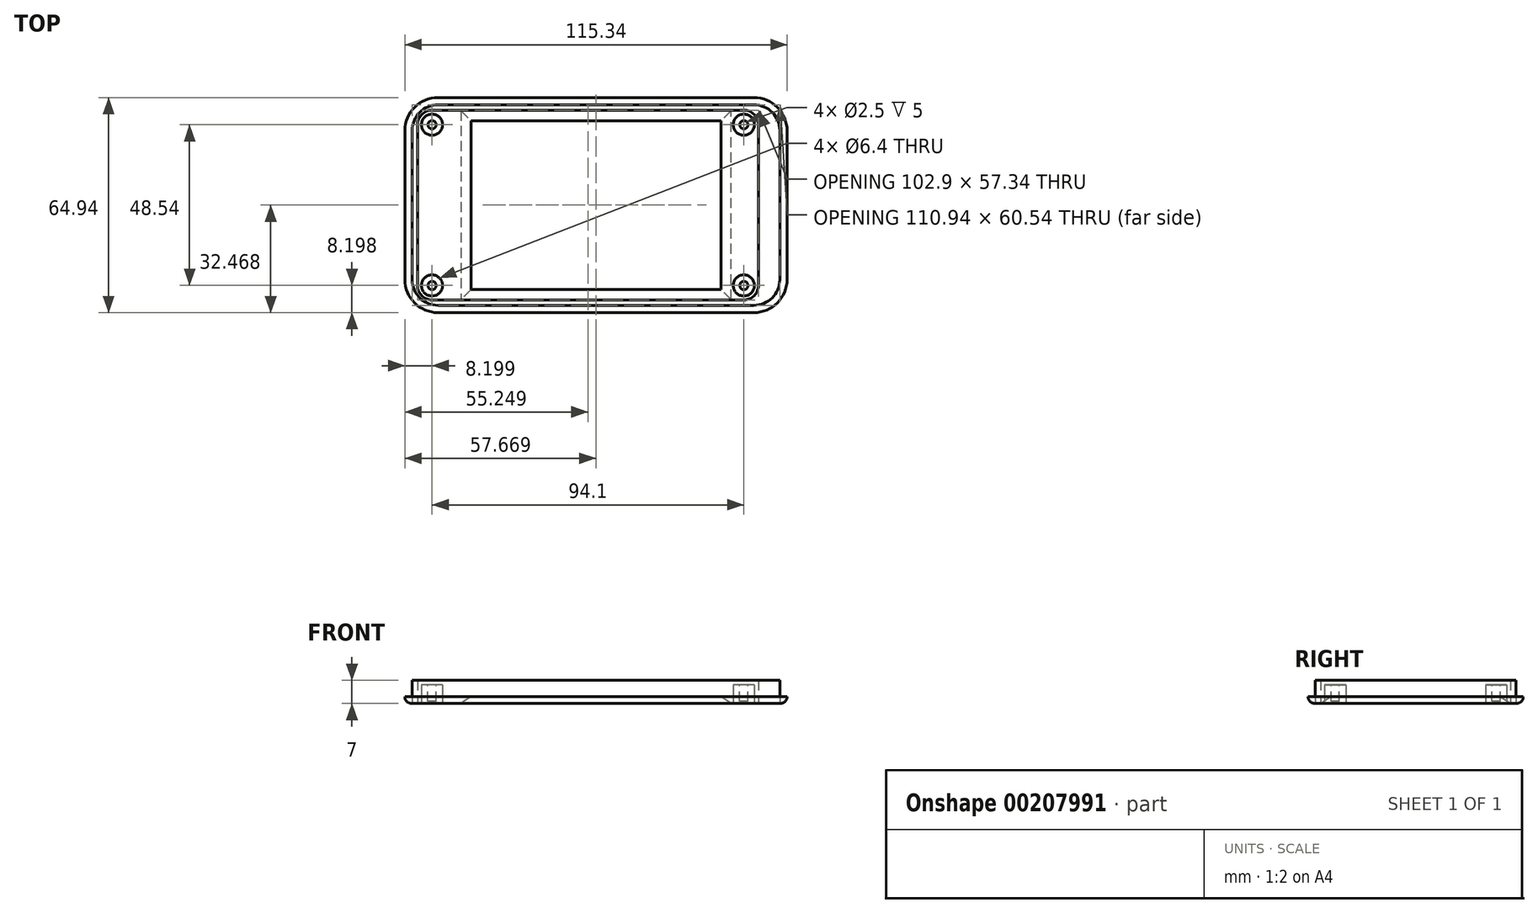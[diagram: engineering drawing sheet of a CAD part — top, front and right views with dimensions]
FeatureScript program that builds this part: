
annotation { "Feature Type Name" : "Feature", "Feature Type Description" : "" }
export const myFeature = defineFeature(function(context is Context, id is Id, definition is map)
    precondition{}
    {
        {
            var Q0;
            Q0=qCreatedBy(makeId("Top.planeOp"),FACE);
            var sketch = newSketch(context, id + "F0", { "sketchPlane" : qUnion([Q0])});
            skCircle(sketch, "E0", {"center": v(-31.24, 28.46) * mm, "radius": 3.2 * mm});
            skCircle(sketch, "E1", {"center": v(62.86, 28.46) * mm, "radius": 3.2 * mm});
            skCircle(sketch, "E2", {"center": v(62.86, -20.08) * mm, "radius": 3.2 * mm});
            skCircle(sketch, "E3", {"center": v(-31.24, -20.08) * mm, "radius": 3.2 * mm});
            skLineSegment(sketch, "E4.bottom", {"start": v(-31.24, 31.66) * mm, "end": v(62.86, 31.66) * mm});
            skLineSegment(sketch, "E4.top", {"start": v(-31.24, -23.28) * mm, "end": v(62.86, -23.28) * mm});
            skLineSegment(sketch, "E4.left", {"start": v(-34.44, 28.46) * mm, "end": v(-34.44, -20.08) * mm});
            skLineSegment(sketch, "E4.right", {"start": v(66.06, 28.46) * mm, "end": v(66.06, -20.08) * mm});
            skLineSegment(sketch, "E5.bottom", {"start": v(-19.52, 29.69) * mm, "end": v(55.98, 29.69) * mm});
            skLineSegment(sketch, "E5.top", {"start": v(-19.52, -21.31) * mm, "end": v(55.98, -21.31) * mm});
            skLineSegment(sketch, "E5.left", {"start": v(-19.52, 29.69) * mm, "end": v(-19.52, -21.31) * mm});
            skLineSegment(sketch, "E5.right", {"start": v(55.98, 29.69) * mm, "end": v(55.98, -21.31) * mm});
            skLineSegment(sketch, "E6.bottom", {"start": v(-29.44, 36.66) * mm, "end": v(65.9, 36.66) * mm});
            skLineSegment(sketch, "E6.top", {"start": v(-29.44, -28.28) * mm, "end": v(65.9, -28.28) * mm});
            skLineSegment(sketch, "E6.left", {"start": v(-39.44, 26.66) * mm, "end": v(-39.44, -18.28) * mm});
            skLineSegment(sketch, "E6.right", {"start": v(75.9, 26.66) * mm, "end": v(75.9, -18.28) * mm});
            skPoint(sketch, "E7.centerSnap0", {"position": v(18.23, -21.31) * mm});
            skPoint(sketch, "E7.centerSnap1", {"position": v(-19.52, 4.19) * mm});
            skPoint(sketch, "E8.visualSharp", {"position": v(-39.44, 36.66) * mm});
            skArc(sketch, "E8.filletArc", {"start": v(-29.44, 36.66) * mm, "mid": v(-36.51, 33.73) * mm, "end": v(-39.44, 26.66) * mm});
            skPoint(sketch, "E9.visualSharp", {"position": v(-39.44, -28.28) * mm});
            skArc(sketch, "E9.filletArc", {"start": v(-39.44, -18.28) * mm, "mid": v(-36.51, -25.35) * mm, "end": v(-29.44, -28.28) * mm});
            skPoint(sketch, "E10.visualSharp", {"position": v(75.9, -28.28) * mm});
            skArc(sketch, "E10.filletArc", {"start": v(65.9, -28.28) * mm, "mid": v(72.97, -25.35) * mm, "end": v(75.9, -18.28) * mm});
            skPoint(sketch, "E11.visualSharp", {"position": v(75.9, 36.66) * mm});
            skArc(sketch, "E11.filletArc", {"start": v(75.9, 26.66) * mm, "mid": v(72.97, 33.73) * mm, "end": v(65.9, 36.66) * mm});
            skPoint(sketch, "E12.visualSharp", {"position": v(66.06, 31.66) * mm});
            skArc(sketch, "E12.filletArc", {"start": v(66.06, 28.46) * mm, "mid": v(65.12, 30.72) * mm, "end": v(62.86, 31.66) * mm});
            skPoint(sketch, "E13.visualSharp", {"position": v(66.06, -23.28) * mm});
            skArc(sketch, "E13.filletArc", {"start": v(62.86, -23.28) * mm, "mid": v(65.12, -22.34) * mm, "end": v(66.06, -20.08) * mm});
            skPoint(sketch, "E14.visualSharp", {"position": v(-34.44, -23.28) * mm});
            skArc(sketch, "E14.filletArc", {"start": v(-34.44, -20.08) * mm, "mid": v(-33.5, -22.34) * mm, "end": v(-31.24, -23.28) * mm});
            skPoint(sketch, "E15.visualSharp", {"position": v(-34.44, 31.66) * mm});
            skArc(sketch, "E15.filletArc", {"start": v(-31.24, 31.66) * mm, "mid": v(-33.5, 30.72) * mm, "end": v(-34.44, 28.46) * mm});
            skArc(sketch, "E16.0", {"start": v(-29.44, 34.46) * mm, "mid": v(-34.96, 32.17) * mm, "end": v(-37.24, 26.66) * mm});
            skLineSegment(sketch, "E16.1", {"start": v(-37.24, 26.66) * mm, "end": v(-37.24, -18.28) * mm});
            skLineSegment(sketch, "E16.2", {"start": v(-29.44, 34.46) * mm, "end": v(65.9, 34.46) * mm});
            skArc(sketch, "E16.3", {"start": v(-37.24, -18.28) * mm, "mid": v(-34.96, -23.8) * mm, "end": v(-29.44, -26.08) * mm});
            skArc(sketch, "E16.4", {"start": v(73.7, 26.66) * mm, "mid": v(71.41, 32.17) * mm, "end": v(65.9, 34.46) * mm});
            skLineSegment(sketch, "E16.5", {"start": v(73.7, 26.66) * mm, "end": v(73.7, -18.28) * mm});
            skArc(sketch, "E16.6", {"start": v(65.9, -26.08) * mm, "mid": v(71.41, -23.8) * mm, "end": v(73.7, -18.28) * mm});
            skLineSegment(sketch, "E16.7", {"start": v(-29.44, -26.08) * mm, "end": v(65.9, -26.08) * mm});
            skArc(sketch, "E17.0", {"start": v(67.26, 28.46) * mm, "mid": v(65.97, 31.57) * mm, "end": v(62.86, 32.86) * mm});
            skLineSegment(sketch, "E17.1", {"start": v(-31.24, 32.86) * mm, "end": v(62.86, 32.86) * mm});
            skLineSegment(sketch, "E17.2", {"start": v(67.26, 28.46) * mm, "end": v(67.26, -20.08) * mm});
            skArc(sketch, "E17.3", {"start": v(-31.24, 32.86) * mm, "mid": v(-34.35, 31.57) * mm, "end": v(-35.64, 28.46) * mm});
            skArc(sketch, "E17.4", {"start": v(62.86, -24.48) * mm, "mid": v(65.97, -23.2) * mm, "end": v(67.26, -20.08) * mm});
            skLineSegment(sketch, "E17.5", {"start": v(-31.24, -24.48) * mm, "end": v(62.86, -24.48) * mm});
            skArc(sketch, "E17.6", {"start": v(-35.64, -20.08) * mm, "mid": v(-34.35, -23.2) * mm, "end": v(-31.24, -24.48) * mm});
            skLineSegment(sketch, "E17.7", {"start": v(-35.64, 28.46) * mm, "end": v(-35.64, -20.08) * mm});
            skSolve(sketch);
        }
        {
            var Q0;
            {var subQ0=sQuery(id+"F0.wireOp",EDGE,"E0");var subQ1=makeQuery(id+"F0.imprint","INTERSECT",VERTEX,{"derivedFrom":[subQ0,sQuery(id+"F0.wireOp",EDGE,"E4.bottom")]});Q0=makeQuery(id+"F0.imprint","IMPRINT",FACE,{"disambiguationData":[TD([[makeQuery(id+"F0.imprint","IMPRINT",EDGE,{"disambiguationData":[TD([[subQ1,-1.0]])],"derivedFrom":subQ0}),1.0]])]});}
            var Q1;
            {var subQ0=sQuery(id+"F0.wireOp",EDGE,"E3");var subQ1=makeQuery(id+"F0.imprint","INTERSECT",VERTEX,{"derivedFrom":[subQ0,sQuery(id+"F0.wireOp",EDGE,"E4.top")]});Q1=makeQuery(id+"F0.imprint","IMPRINT",FACE,{"disambiguationData":[TD([[makeQuery(id+"F0.imprint","IMPRINT",EDGE,{"disambiguationData":[TD([[subQ1,1.0]])],"derivedFrom":subQ0}),1.0]])]});}
            var Q2;
            {var subQ0=sQuery(id+"F0.wireOp",EDGE,"E2");var subQ1=makeQuery(id+"F0.imprint","INTERSECT",VERTEX,{"derivedFrom":[subQ0,sQuery(id+"F0.wireOp",EDGE,"E4.top")]});Q2=makeQuery(id+"F0.imprint","IMPRINT",FACE,{"disambiguationData":[TD([[makeQuery(id+"F0.imprint","IMPRINT",EDGE,{"disambiguationData":[TD([[subQ1,1.0]])],"derivedFrom":subQ0}),1.0]])]});}
            var Q3;
            {var subQ0=sQuery(id+"F0.wireOp",EDGE,"E1");var subQ1=makeQuery(id+"F0.imprint","INTERSECT",VERTEX,{"derivedFrom":[subQ0,sQuery(id+"F0.wireOp",EDGE,"E4.bottom")]});Q3=makeQuery(id+"F0.imprint","IMPRINT",FACE,{"disambiguationData":[TD([[makeQuery(id+"F0.imprint","IMPRINT",EDGE,{"disambiguationData":[TD([[subQ1,1.0]])],"derivedFrom":subQ0}),1.0]])]});}
            extrude(context, id + "F1", {"entities" : qUnion([Q0, Q1, Q2, Q3]), "depth" : 5.6 * mm});
        }
        {
            var Q0;
            Q0=makeQuery(id+"F0.imprint","IMPRINT",FACE,{"disambiguationData":[TD([[makeQuery(id+"F0.imprint","IMPRINT",EDGE,{"derivedFrom":sQuery(id+"F0.wireOp",EDGE,"E16.0")}),1.0]])]});
            extrude(context, id + "F2", {"entities" : qUnion([Q0]), "depth" : 7 * mm});
        }
        {
            var Q0;
            Q0=makeQuery(id+"F0.imprint","IMPRINT",FACE,{"disambiguationData":[TD([[makeQuery(id+"F0.imprint","IMPRINT",EDGE,{"derivedFrom":sQuery(id+"F0.wireOp",EDGE,"E5.bottom")}),1.0]])]});
            var Q1;
            Q1=makeQuery(id+"F0.imprint","IMPRINT",FACE,{"disambiguationData":[TD([[makeQuery(id+"F0.imprint","IMPRINT",EDGE,{"derivedFrom":sQuery(id+"F0.wireOp",EDGE,"E17.0")}),1.0]])]});
            var Q2;
            Q2=makeQuery(id+"F0.imprint","IMPRINT",FACE,{"disambiguationData":[TD([[makeQuery(id+"F0.imprint","IMPRINT",EDGE,{"derivedFrom":sQuery(id+"F0.wireOp",EDGE,"E6.bottom")}),-1.0]])]});
            extrude(context, id + "F3", {"entities" : qUnion([Q0, Q1, Q2]), "depth" : 2 * mm});
        }
        {
            var Q0;
            Q0=makeQuery(id+"F3.opExtrude","CAP_EDGE",EDGE,{"disambiguationData":[OSD([sQuery(id+"F0.wireOp",EDGE,"E9.filletArc")])],"isStart":true});
            fillet(context, id + "F4", {"entities" : qUnion([Q0]), "radius" : 2 * mm, "tangentPropagation" : true, "allowEdgeOverflow" : false});
        }
        {
            var Q0;
            Q0=makeQuery(id+"F3.opExtrude","CAP_EDGE",EDGE,{"disambiguationData":[OSD([sQuery(id+"F0.wireOp",EDGE,"E5.bottom")])],"isStart":true});
            var Q1;
            Q1=makeQuery(id+"F3.opExtrude","CAP_EDGE",EDGE,{"disambiguationData":[OSD([sQuery(id+"F0.wireOp",EDGE,"E5.left")])],"isStart":true});
            var Q2;
            Q2=makeQuery(id+"F3.opExtrude","CAP_EDGE",EDGE,{"disambiguationData":[OSD([sQuery(id+"F0.wireOp",EDGE,"E5.top")])],"isStart":true});
            var Q3;
            Q3=makeQuery(id+"F3.opExtrude","CAP_EDGE",EDGE,{"disambiguationData":[OSD([sQuery(id+"F0.wireOp",EDGE,"E5.right")])],"isStart":true});
            chamfer(context, id + "F5", {"entities" : qUnion([Q0, Q1, Q2, Q3]), "chamferType" : ChamferType.TWO_OFFSETS, "width1" : 2 * mm, "oppositeDirection" : false, "width2" : 3 * mm, "tangentPropagation" : true});
        }
        {
            var Q0;
            Q0=makeQuery(id+"F1.opExtrude","CAP_FACE",FACE,{"disambiguationData":[OSD([sQuery(id+"F0.wireOp",EDGE,"E2"),sQuery(id+"F0.wireOp",EDGE,"E4.top"),sQuery(id+"F0.wireOp",EDGE,"E4.right"),sQuery(id+"F0.wireOp",EDGE,"E13.filletArc")])],"isStart":false});
            var sketch = newSketch(context, id + "F6", { "sketchPlane" : qUnion([Q0])});
            skCircle(sketch, "E18", {"center": v(62.86, 28.46) * mm, "radius": 1.25 * mm});
            skCircle(sketch, "E19", {"center": v(62.86, -20.08) * mm, "radius": 1.25 * mm});
            skCircle(sketch, "E20", {"center": v(-31.24, 28.46) * mm, "radius": 1.25 * mm});
            skCircle(sketch, "E21", {"center": v(-31.24, -20.08) * mm, "radius": 1.25 * mm});
            skSolve(sketch);
        }
        {
            var Q0;
            Q0=makeQuery(id+"F6.imprint","IMPRINT",FACE,{"disambiguationData":[TD([[makeQuery(id+"F6.imprint","IMPRINT",EDGE,{"derivedFrom":sQuery(id+"F6.wireOp",EDGE,"E20")}),1.0]])]});
            var Q1;
            Q1=makeQuery(id+"F6.imprint","IMPRINT",FACE,{"disambiguationData":[TD([[makeQuery(id+"F6.imprint","IMPRINT",EDGE,{"derivedFrom":sQuery(id+"F6.wireOp",EDGE,"E21")}),1.0]])]});
            var Q2;
            Q2=makeQuery(id+"F6.imprint","IMPRINT",FACE,{"disambiguationData":[TD([[makeQuery(id+"F6.imprint","IMPRINT",EDGE,{"derivedFrom":sQuery(id+"F6.wireOp",EDGE,"E19")}),1.0]])]});
            var Q3;
            Q3=makeQuery(id+"F6.imprint","IMPRINT",FACE,{"disambiguationData":[TD([[makeQuery(id+"F6.imprint","IMPRINT",EDGE,{"derivedFrom":sQuery(id+"F6.wireOp",EDGE,"E18")}),1.0]])]});
            extrude(context, id + "F7", {"entities" : qUnion([Q0, Q1, Q2, Q3]), "operationType" : NewBodyOperationType.REMOVE, "oppositeDirection" : true, "depth" : 5 * mm});
        }
    });
